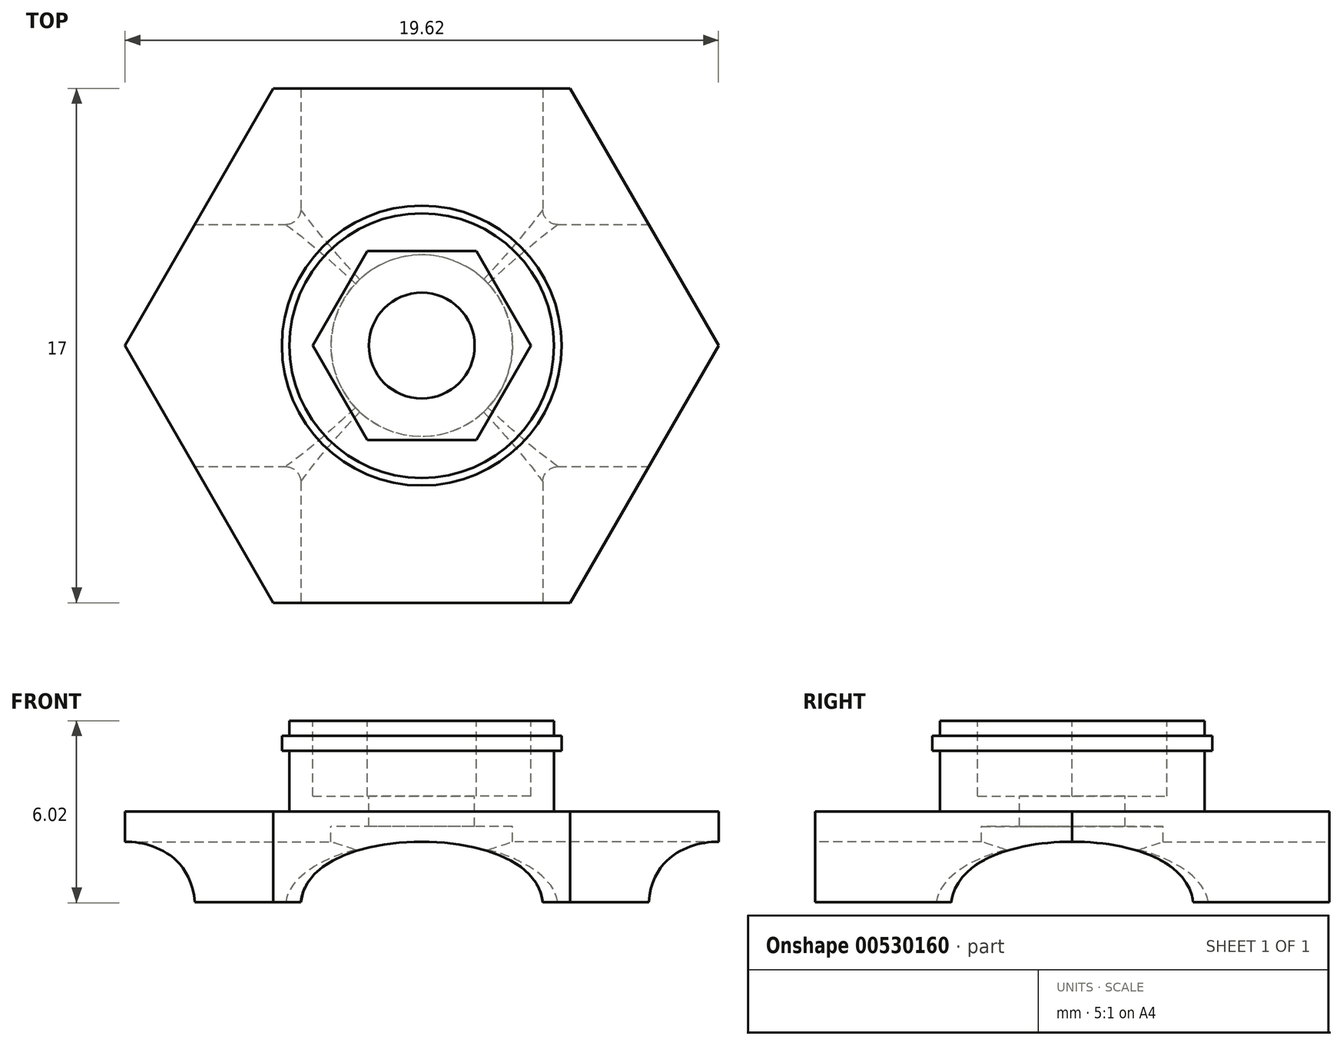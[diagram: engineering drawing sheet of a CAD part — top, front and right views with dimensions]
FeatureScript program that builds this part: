
annotation { "Feature Type Name" : "Feature", "Feature Type Description" : "" }
export const myFeature = defineFeature(function(context is Context, id is Id, definition is map)
    precondition{}
    {
        {
            var Q0;
            Q0=qCreatedBy(makeId("Top.planeOp"),FACE);
            var sketch = newSketch(context, id + "F0", { "sketchPlane" : qUnion([Q0])});
            skCircle(sketch, "E0.cCircle", {"center": v(0, 0) * mm, "radius": 8.5 * mm, "construction": true});
            skLineSegment(sketch, "E0.0", {"start": v(-4.9, 8.5) * mm, "end": v(4.9, 8.5) * mm});
            skLineSegment(sketch, "E0.1", {"start": v(4.9, 8.5) * mm, "end": v(9.81, 0) * mm});
            skLineSegment(sketch, "E0.2", {"start": v(9.81, 0) * mm, "end": v(4.9, -8.5) * mm});
            skLineSegment(sketch, "E0.3", {"start": v(4.9, -8.5) * mm, "end": v(-4.9, -8.5) * mm});
            skLineSegment(sketch, "E0.4", {"start": v(-4.9, -8.5) * mm, "end": v(-9.81, 0) * mm});
            skLineSegment(sketch, "E0.5", {"start": v(-9.81, 0) * mm, "end": v(-4.9, 8.5) * mm});
            skPoint(sketch, "E0.0.midPoint", {"position": v(0, 8.5) * mm});
            skSolve(sketch);
        }
        {
            var Q0;
            Q0=makeQuery(id+"F0.imprint","IMPRINT",FACE,{"disambiguationData":[TD([[makeQuery(id+"F0.imprint","IMPRINT",EDGE,{"derivedFrom":sQuery(id+"F0.wireOp",EDGE,"E0.0")}),-1.0]])]});
            extrude(context, id + "F1", {"entities" : qUnion([Q0]), "depth" : 3 * mm, "offsetDistance" : 25 * mm});
        }
        {
            var Q0;
            Q0=makeQuery(id+"F1.opExtrude","CAP_FACE",FACE,{"disambiguationData":[OSD([sQuery(id+"F0.wireOp",EDGE,"E0.0"),sQuery(id+"F0.wireOp",EDGE,"E0.1"),sQuery(id+"F0.wireOp",EDGE,"E0.2"),sQuery(id+"F0.wireOp",EDGE,"E0.3"),sQuery(id+"F0.wireOp",EDGE,"E0.4"),sQuery(id+"F0.wireOp",EDGE,"E0.5")])],"isStart":false});
            var sketch = newSketch(context, id + "F2", { "sketchPlane" : qUnion([Q0])});
            skCircle(sketch, "E1", {"center": v(0, 0) * mm, "radius": 4.38 * mm});
            skCircle(sketch, "E2", {"center": v(0, 0) * mm, "radius": 4.63 * mm});
            skSolve(sketch);
        }
        {
            var Q0;
            Q0=makeQuery(id+"F2.imprint","IMPRINT",FACE,{"disambiguationData":[TD([[makeQuery(id+"F2.imprint","IMPRINT",EDGE,{"derivedFrom":sQuery(id+"F2.wireOp",EDGE,"E1")}),1.0]])]});
            extrude(context, id + "F3", {"entities" : qUnion([Q0]), "operationType" : NewBodyOperationType.ADD, "depth" : 3 * mm, "offsetDistance" : 25 * mm});
        }
        {
            var Q0;
            Q0=makeQuery(id+"F2.imprint","IMPRINT",FACE,{"disambiguationData":[TD([[makeQuery(id+"F2.imprint","IMPRINT",EDGE,{"derivedFrom":sQuery(id+"F2.wireOp",EDGE,"E1")}),-1.0]])]});
            extrude(context, id + "F4", {"entities" : qUnion([Q0]), "operationType" : NewBodyOperationType.ADD, "depth" : 2.5 * mm, "offsetDistance" : 25 * mm, "hasSecondDirection" : true, "secondDirectionOppositeDirection" : false, "secondDirectionDepth" : 2 * mm});
        }
        {
            var Q0;
            Q0=makeQuery(id+"F3.opExtrude","CAP_FACE",FACE,{"disambiguationData":[OSD([sQuery(id+"F2.wireOp",EDGE,"E1")])],"isStart":false});
            var sketch = newSketch(context, id + "F5", { "sketchPlane" : qUnion([Q0])});
            skCircle(sketch, "E3.cCircle", {"center": v(0, 0) * mm, "radius": 3.12 * mm, "construction": true});
            skLineSegment(sketch, "E3.0", {"start": v(-1.8, 3.12) * mm, "end": v(1.8, 3.12) * mm});
            skLineSegment(sketch, "E3.1", {"start": v(1.8, 3.12) * mm, "end": v(3.6, 0) * mm});
            skLineSegment(sketch, "E3.2", {"start": v(3.6, 0) * mm, "end": v(1.8, -3.12) * mm});
            skLineSegment(sketch, "E3.3", {"start": v(1.8, -3.12) * mm, "end": v(-1.8, -3.13) * mm});
            skLineSegment(sketch, "E3.4", {"start": v(-1.8, -3.13) * mm, "end": v(-3.6, 0) * mm});
            skLineSegment(sketch, "E3.5", {"start": v(-3.6, 0) * mm, "end": v(-1.8, 3.12) * mm});
            skPoint(sketch, "E3.0.midPoint", {"position": v(0, 3.12) * mm});
            skSolve(sketch);
        }
        {
            var Q0;
            Q0=makeQuery(id+"F5.imprint","IMPRINT",FACE,{"disambiguationData":[TD([[makeQuery(id+"F5.imprint","IMPRINT",EDGE,{"derivedFrom":sQuery(id+"F5.wireOp",EDGE,"E3.0")}),-1.0]])]});
            extrude(context, id + "F6", {"entities" : qUnion([Q0]), "operationType" : NewBodyOperationType.REMOVE, "oppositeDirection" : true, "depth" : 2.5 * mm, "offsetDistance" : 25 * mm});
        }
        {
            var Q0;
            Q0=makeQuery(id+"F3.opExtrude","CAP_FACE",FACE,{"disambiguationData":[OSD([sQuery(id+"F2.wireOp",EDGE,"E1")])],"isStart":false});
            var sketch = newSketch(context, id + "F7", { "sketchPlane" : qUnion([Q0])});
            skCircle(sketch, "E4", {"center": v(0, 0) * mm, "radius": 1.75 * mm});
            skSolve(sketch);
        }
        {
            var Q0;
            Q0=makeQuery(id+"F7.imprint","IMPRINT",FACE,{"disambiguationData":[TD([[makeQuery(id+"F7.imprint","IMPRINT",EDGE,{"derivedFrom":sQuery(id+"F7.wireOp",EDGE,"E4")}),1.0]])]});
            extrude(context, id + "F8", {"entities" : qUnion([Q0]), "operationType" : NewBodyOperationType.REMOVE, "endBound" : BoundingType.THROUGH_ALL, "oppositeDirection" : true, "depth" : 25 * mm, "offsetDistance" : 25 * mm});
        }
        {
            var Q0;
            Q0=makeQuery(id+"F3.opExtrude","CAP_FACE",FACE,{"disambiguationData":[OSD([sQuery(id+"F2.wireOp",EDGE,"E1")])],"isStart":false});
            var sketch = newSketch(context, id + "F9", { "sketchPlane" : qUnion([Q0])});
            skCircle(sketch, "E5", {"center": v(0, 0) * mm, "radius": 3 * mm});
            skSolve(sketch);
        }
        {
            var Q0;
            Q0 = qSketchRegion(id + "F9", true);
            var Q1;
            Q1=makeQuery(id+"F1.opExtrude","CAP_FACE",FACE,{"disambiguationData":[OSD([sQuery(id+"F0.wireOp",EDGE,"E0.0"),sQuery(id+"F0.wireOp",EDGE,"E0.1"),sQuery(id+"F0.wireOp",EDGE,"E0.2"),sQuery(id+"F0.wireOp",EDGE,"E0.3"),sQuery(id+"F0.wireOp",EDGE,"E0.4"),sQuery(id+"F0.wireOp",EDGE,"E0.5")])],"isStart":true});
            extrude(context, id + "F10", {"entities" : qUnion([Q0]), "operationType" : NewBodyOperationType.REMOVE, "endBound" : BoundingType.UP_TO_SURFACE, "oppositeDirection" : true, "depth" : 25 * mm, "endBoundEntityFace" : qUnion([Q1]), "offsetDistance" : 25 * mm, "hasSecondDirection" : true, "secondDirectionOppositeDirection" : true, "secondDirectionDepth" : 3.5 * mm});
        }
        {
            var Q0;
            Q0=qCreatedBy(makeId("Front.planeOp"),FACE);
            var sketch = newSketch(context, id + "F11", { "sketchPlane" : qUnion([Q0])});
            skFitSpline(sketch, "E6", {"points": [v(-4, 0) * mm, v(0, 2) * mm, v(4, 0) * mm, v(0, -4) * mm, v(-4, 0) * mm]});
            skSolve(sketch);
        }
        {
            var Q0;
            Q0 = qSketchRegion(id + "F11", true);
            var Q1;
            Q1=makeQuery(id+"F1.opExtrude","SWEPT_FACE",FACE,{"disambiguationData":[OSD([sQuery(id+"F0.wireOp",EDGE,"E0.0")])]});
            var Q2;
            Q2=makeQuery(id+"F1.opExtrude","SWEPT_FACE",FACE,{"disambiguationData":[OSD([sQuery(id+"F0.wireOp",EDGE,"E0.3")])]});
            extrude(context, id + "F12", {"entities" : qUnion([Q0]), "operationType" : NewBodyOperationType.REMOVE, "oppositeDirection" : true, "depth" : 25 * mm, "endBoundEntityFace" : qUnion([Q1]), "offsetDistance" : 25 * mm, "symmetric" : true});
        }
        {
            var Q0;
            Q0=qCreatedBy(makeId("Right.planeOp"),FACE);
            var sketch = newSketch(context, id + "F13", { "sketchPlane" : qUnion([Q0])});
            skFitSpline(sketch, "E7", {"points": [v(4, 0) * mm, v(0, 2) * mm, v(-4, 0) * mm, v(0, -4) * mm, v(4, 0) * mm]});
            skSolve(sketch);
        }
        {
            var Q0;
            Q0 = qSketchRegion(id + "F13", true);
            extrude(context, id + "F14", {"entities" : qUnion([Q0]), "operationType" : NewBodyOperationType.REMOVE, "oppositeDirection" : true, "depth" : 25 * mm, "offsetDistance" : 25 * mm, "symmetric" : true});
        }
        {
            var Q0;
            Q0=makeQuery(id+"F14.boolean.opBoolean","SPLIT",EDGE,{"disambiguationData":[OD(1.0)],"derivedFrom":makeQuery(id+"F12.boolean.opBoolean","INTERSECT",EDGE,{"derivedFrom":[makeQuery(id+"F10.boolean.opBoolean","COPY",FACE,{"derivedFrom":makeQuery(id+"F10.opExtrude","SWEPT_FACE",FACE,{"disambiguationData":[OSD([sQuery(id+"F9.wireOp",EDGE,"E5")])]})}),makeQuery(id+"F12.opExtrude","SWEPT_FACE",FACE,{"disambiguationData":[OSD([sQuery(id+"F11.wireOp",EDGE,"nzz4Toy3-Fpa2-iH0y-N5IK-ZllYczAaCJ5c")])]})]})});
            var Q1;
            Q1=makeQuery(id+"F14.boolean.opBoolean","INTERSECT",EDGE,{"disambiguationData":[OD(1.0)],"derivedFrom":[makeQuery(id+"F10.boolean.opBoolean","COPY",FACE,{"derivedFrom":makeQuery(id+"F10.opExtrude","SWEPT_FACE",FACE,{"disambiguationData":[OSD([sQuery(id+"F9.wireOp",EDGE,"E5")])]})}),makeQuery(id+"F14.opExtrude","SWEPT_FACE",FACE,{"disambiguationData":[OSD([sQuery(id+"F13.wireOp",EDGE,"j7p87nXo-q3uN-MPqY-KFCe-d6YkDTyWCxmd")])]})]});
            var Q2;
            Q2=makeQuery(id+"F14.boolean.opBoolean","SPLIT",EDGE,{"disambiguationData":[OD(0.0)],"derivedFrom":makeQuery(id+"F12.boolean.opBoolean","INTERSECT",EDGE,{"derivedFrom":[makeQuery(id+"F10.boolean.opBoolean","COPY",FACE,{"derivedFrom":makeQuery(id+"F10.opExtrude","SWEPT_FACE",FACE,{"disambiguationData":[OSD([sQuery(id+"F9.wireOp",EDGE,"E5")])]})}),makeQuery(id+"F12.opExtrude","SWEPT_FACE",FACE,{"disambiguationData":[OSD([sQuery(id+"F11.wireOp",EDGE,"nzz4Toy3-Fpa2-iH0y-N5IK-ZllYczAaCJ5c")])]})]})});
            var Q3;
            Q3=makeQuery(id+"F14.boolean.opBoolean","INTERSECT",EDGE,{"disambiguationData":[OD(0.0)],"derivedFrom":[makeQuery(id+"F10.boolean.opBoolean","COPY",FACE,{"derivedFrom":makeQuery(id+"F10.opExtrude","SWEPT_FACE",FACE,{"disambiguationData":[OSD([sQuery(id+"F9.wireOp",EDGE,"E5")])]})}),makeQuery(id+"F14.opExtrude","SWEPT_FACE",FACE,{"disambiguationData":[OSD([sQuery(id+"F13.wireOp",EDGE,"j7p87nXo-q3uN-MPqY-KFCe-d6YkDTyWCxmd")])]})]});
            var Q4;
            Q4=makeQuery(id+"F14.boolean.opBoolean","INTERSECT",EDGE,{"disambiguationData":[OD(3.0)],"derivedFrom":[makeQuery(id+"F12.boolean.opBoolean","COPY",FACE,{"derivedFrom":makeQuery(id+"F12.opExtrude","SWEPT_FACE",FACE,{"disambiguationData":[OSD([sQuery(id+"F11.wireOp",EDGE,"E6")])]})}),makeQuery(id+"F14.opExtrude","SWEPT_FACE",FACE,{"disambiguationData":[OSD([sQuery(id+"F13.wireOp",EDGE,"E7")])]})]});
            var Q5;
            Q5=makeQuery(id+"F14.boolean.opBoolean","INTERSECT",EDGE,{"disambiguationData":[OD(1.0)],"derivedFrom":[makeQuery(id+"F12.boolean.opBoolean","COPY",FACE,{"derivedFrom":makeQuery(id+"F12.opExtrude","SWEPT_FACE",FACE,{"disambiguationData":[OSD([sQuery(id+"F11.wireOp",EDGE,"E6")])]})}),makeQuery(id+"F14.opExtrude","SWEPT_FACE",FACE,{"disambiguationData":[OSD([sQuery(id+"F13.wireOp",EDGE,"E7")])]})]});
            var Q6;
            Q6=makeQuery(id+"F14.boolean.opBoolean","INTERSECT",EDGE,{"disambiguationData":[OD(2.0)],"derivedFrom":[makeQuery(id+"F12.boolean.opBoolean","COPY",FACE,{"derivedFrom":makeQuery(id+"F12.opExtrude","SWEPT_FACE",FACE,{"disambiguationData":[OSD([sQuery(id+"F11.wireOp",EDGE,"E6")])]})}),makeQuery(id+"F14.opExtrude","SWEPT_FACE",FACE,{"disambiguationData":[OSD([sQuery(id+"F13.wireOp",EDGE,"E7")])]})]});
            var Q7;
            Q7=makeQuery(id+"F14.boolean.opBoolean","INTERSECT",EDGE,{"disambiguationData":[OD(0.0)],"derivedFrom":[makeQuery(id+"F12.boolean.opBoolean","COPY",FACE,{"derivedFrom":makeQuery(id+"F12.opExtrude","SWEPT_FACE",FACE,{"disambiguationData":[OSD([sQuery(id+"F11.wireOp",EDGE,"E6")])]})}),makeQuery(id+"F14.opExtrude","SWEPT_FACE",FACE,{"disambiguationData":[OSD([sQuery(id+"F13.wireOp",EDGE,"E7")])]})]});
            fillet(context, id + "F15", {"entities" : qUnion([Q0, Q1, Q2, Q3, Q4, Q5, Q6, Q7]), "tangentPropagation" : true, "radius" : 0.5 * mm, "defaultsChanged" : false, "vertexSettings" : [], "allowEdgeOverflow" : false});
        }
    });
